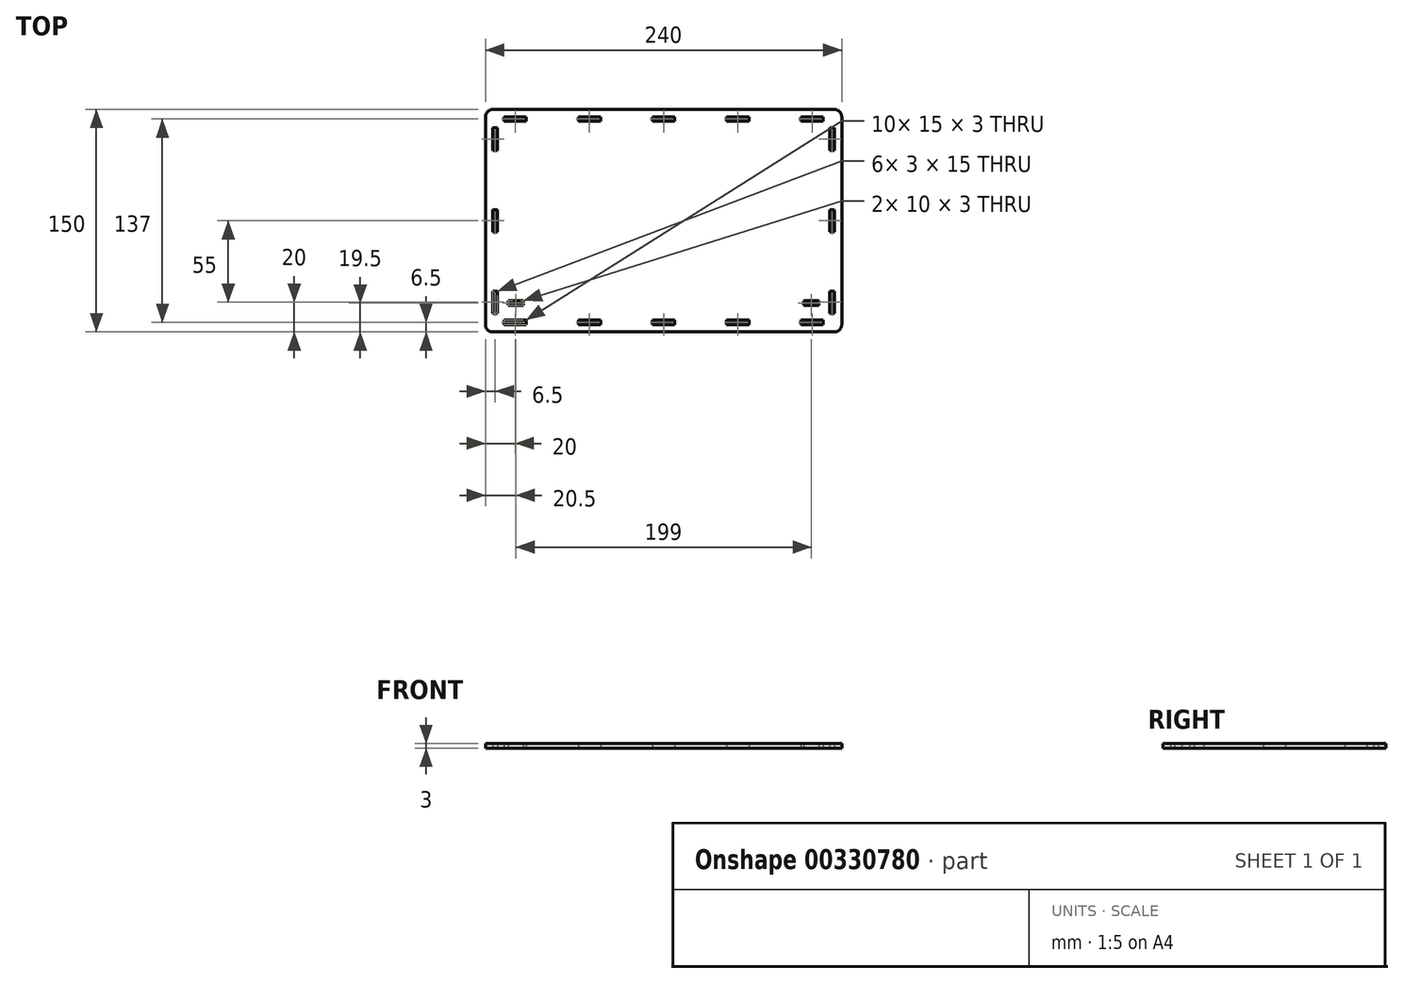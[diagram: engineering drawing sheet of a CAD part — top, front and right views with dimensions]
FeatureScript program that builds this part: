
annotation { "Feature Type Name" : "Feature", "Feature Type Description" : "" }
export const myFeature = defineFeature(function(context is Context, id is Id, definition is map)
    precondition{}
    {
        {
            var Q0;
            Q0=qCreatedBy(makeId("Top.planeOp"),FACE);
            var sketch = newSketch(context, id + "F0", { "sketchPlane" : qUnion([Q0])});
            skLineSegment(sketch, "E0.bottom", {"start": v(115, 75) * mm, "end": v(-115, 75) * mm});
            skLineSegment(sketch, "E0.top", {"start": v(115, -75) * mm, "end": v(-115, -75) * mm});
            skLineSegment(sketch, "E0.left", {"start": v(120, 70) * mm, "end": v(120, -70) * mm});
            skLineSegment(sketch, "E0.right", {"start": v(-120, 70) * mm, "end": v(-120, -70) * mm});
            skPoint(sketch, "E0.middle", {"position": v(0, 0) * mm});
            skLineSegment(sketch, "E1.bottom", {"start": v(-107.5, 70) * mm, "end": v(-92.5, 70) * mm});
            skLineSegment(sketch, "E1.top", {"start": v(-107.5, 67) * mm, "end": v(-92.5, 67) * mm});
            skLineSegment(sketch, "E1.left", {"start": v(-107.5, 70) * mm, "end": v(-107.5, 67) * mm});
            skLineSegment(sketch, "E1.right", {"start": v(-92.5, 70) * mm, "end": v(-92.5, 67) * mm});
            skLineSegment(sketch, "E2.0.1.0", {"start": v(-107.5, -67) * mm, "end": v(-107.5, -70) * mm});
            skLineSegment(sketch, "E2.0.1.1", {"start": v(-107.5, -67) * mm, "end": v(-92.5, -67) * mm});
            skLineSegment(sketch, "E2.0.1.2", {"start": v(-92.5, -67) * mm, "end": v(-92.5, -70) * mm});
            skLineSegment(sketch, "E2.0.1.3", {"start": v(-107.5, -70) * mm, "end": v(-92.5, -70) * mm});
            skLineSegment(sketch, "E2.1.0.0", {"start": v(-57.5, 70) * mm, "end": v(-57.5, 67) * mm});
            skLineSegment(sketch, "E2.1.0.1", {"start": v(-57.5, 70) * mm, "end": v(-42.5, 70) * mm});
            skLineSegment(sketch, "E2.1.0.2", {"start": v(-42.5, 70) * mm, "end": v(-42.5, 67) * mm});
            skLineSegment(sketch, "E2.1.0.3", {"start": v(-57.5, 67) * mm, "end": v(-42.5, 67) * mm});
            skLineSegment(sketch, "E2.1.1.0", {"start": v(-57.5, -67) * mm, "end": v(-57.5, -70) * mm});
            skLineSegment(sketch, "E2.1.1.1", {"start": v(-57.5, -67) * mm, "end": v(-42.5, -67) * mm});
            skLineSegment(sketch, "E2.1.1.2", {"start": v(-42.5, -67) * mm, "end": v(-42.5, -70) * mm});
            skLineSegment(sketch, "E2.1.1.3", {"start": v(-57.5, -70) * mm, "end": v(-42.5, -70) * mm});
            skLineSegment(sketch, "E2.2.0.0", {"start": v(-7.5, 70) * mm, "end": v(-7.5, 67) * mm});
            skLineSegment(sketch, "E2.2.0.1", {"start": v(-7.5, 70) * mm, "end": v(7.5, 70) * mm});
            skLineSegment(sketch, "E2.2.0.2", {"start": v(7.5, 70) * mm, "end": v(7.5, 67) * mm});
            skLineSegment(sketch, "E2.2.0.3", {"start": v(-7.5, 67) * mm, "end": v(7.5, 67) * mm});
            skLineSegment(sketch, "E2.2.1.0", {"start": v(-7.5, -67) * mm, "end": v(-7.5, -70) * mm});
            skLineSegment(sketch, "E2.2.1.1", {"start": v(-7.5, -67) * mm, "end": v(7.5, -67) * mm});
            skLineSegment(sketch, "E2.2.1.2", {"start": v(7.5, -67) * mm, "end": v(7.5, -70) * mm});
            skLineSegment(sketch, "E2.2.1.3", {"start": v(-7.5, -70) * mm, "end": v(7.5, -70) * mm});
            skLineSegment(sketch, "E2.3.0.0", {"start": v(42.5, 70) * mm, "end": v(42.5, 67) * mm});
            skLineSegment(sketch, "E2.3.0.1", {"start": v(42.5, 70) * mm, "end": v(57.5, 70) * mm});
            skLineSegment(sketch, "E2.3.0.2", {"start": v(57.5, 70) * mm, "end": v(57.5, 67) * mm});
            skLineSegment(sketch, "E2.3.0.3", {"start": v(42.5, 67) * mm, "end": v(57.5, 67) * mm});
            skLineSegment(sketch, "E2.3.1.0", {"start": v(42.5, -67) * mm, "end": v(42.5, -70) * mm});
            skLineSegment(sketch, "E2.3.1.1", {"start": v(42.5, -67) * mm, "end": v(57.5, -67) * mm});
            skLineSegment(sketch, "E2.3.1.2", {"start": v(57.5, -67) * mm, "end": v(57.5, -70) * mm});
            skLineSegment(sketch, "E2.3.1.3", {"start": v(42.5, -70) * mm, "end": v(57.5, -70) * mm});
            skLineSegment(sketch, "E2.direction1", {"start": v(-107.5, 67) * mm, "end": v(-57.5, 67) * mm, "construction": true});
            skLineSegment(sketch, "E2.direction2", {"start": v(-107.5, 67) * mm, "end": v(-107.5, -70) * mm, "construction": true});
            skLineSegment(sketch, "E3.0.4.0", {"start": v(92.5, 70) * mm, "end": v(92.5, 67) * mm});
            skLineSegment(sketch, "E3.3.4.0", {"start": v(92.5, 70) * mm, "end": v(107.5, 70) * mm});
            skLineSegment(sketch, "E3.6.4.0", {"start": v(107.5, 70) * mm, "end": v(107.5, 67) * mm});
            skLineSegment(sketch, "E3.9.4.0", {"start": v(92.5, 67) * mm, "end": v(107.5, 67) * mm});
            skLineSegment(sketch, "E3.0.4.1", {"start": v(92.5, -67) * mm, "end": v(92.5, -70) * mm});
            skLineSegment(sketch, "E3.3.4.1", {"start": v(92.5, -67) * mm, "end": v(107.5, -67) * mm});
            skLineSegment(sketch, "E3.6.4.1", {"start": v(107.5, -67) * mm, "end": v(107.5, -70) * mm});
            skLineSegment(sketch, "E3.9.4.1", {"start": v(92.5, -70) * mm, "end": v(107.5, -70) * mm});
            skPoint(sketch, "E4.visualSharp", {"position": v(-120, 75) * mm});
            skArc(sketch, "E4.filletArc", {"start": v(-115, 75) * mm, "mid": v(-118.54, 73.54) * mm, "end": v(-120, 70) * mm});
            skPoint(sketch, "E5.visualSharp", {"position": v(-120, -75) * mm});
            skArc(sketch, "E5.filletArc", {"start": v(-120, -70) * mm, "mid": v(-118.54, -73.54) * mm, "end": v(-115, -75) * mm});
            skPoint(sketch, "E6.visualSharp", {"position": v(120, -75) * mm});
            skArc(sketch, "E6.filletArc", {"start": v(115, -75) * mm, "mid": v(118.54, -73.54) * mm, "end": v(120, -70) * mm});
            skPoint(sketch, "E7.visualSharp", {"position": v(120, 75) * mm});
            skArc(sketch, "E7.filletArc", {"start": v(120, 70) * mm, "mid": v(118.54, 73.54) * mm, "end": v(115, 75) * mm});
            skLineSegment(sketch, "E8.bottom", {"start": v(112, 62.5) * mm, "end": v(115, 62.5) * mm});
            skLineSegment(sketch, "E8.top", {"start": v(112, 47.5) * mm, "end": v(115, 47.5) * mm});
            skLineSegment(sketch, "E8.left", {"start": v(112, 62.5) * mm, "end": v(112, 47.5) * mm});
            skLineSegment(sketch, "E8.right", {"start": v(115, 62.5) * mm, "end": v(115, 47.5) * mm});
            skLineSegment(sketch, "E9.0.1.0", {"start": v(112, 7.5) * mm, "end": v(115, 7.5) * mm});
            skLineSegment(sketch, "E9.0.1.1", {"start": v(115, 7.5) * mm, "end": v(115, -7.5) * mm});
            skLineSegment(sketch, "E9.0.1.2", {"start": v(112, -7.5) * mm, "end": v(115, -7.5) * mm});
            skLineSegment(sketch, "E9.0.1.3", {"start": v(112, 7.5) * mm, "end": v(112, -7.5) * mm});
            skLineSegment(sketch, "E9.0.2.0", {"start": v(112, -47.5) * mm, "end": v(115, -47.5) * mm});
            skLineSegment(sketch, "E9.0.2.1", {"start": v(115, -47.5) * mm, "end": v(115, -62.5) * mm});
            skLineSegment(sketch, "E9.0.2.2", {"start": v(112, -62.5) * mm, "end": v(115, -62.5) * mm});
            skLineSegment(sketch, "E9.0.2.3", {"start": v(112, -47.5) * mm, "end": v(112, -62.5) * mm});
            skLineSegment(sketch, "E9.1.0.0", {"start": v(-115, 62.5) * mm, "end": v(-112, 62.5) * mm});
            skLineSegment(sketch, "E9.1.0.1", {"start": v(-112, 62.5) * mm, "end": v(-112, 47.5) * mm});
            skLineSegment(sketch, "E9.1.0.2", {"start": v(-115, 47.5) * mm, "end": v(-112, 47.5) * mm});
            skLineSegment(sketch, "E9.1.0.3", {"start": v(-115, 62.5) * mm, "end": v(-115, 47.5) * mm});
            skLineSegment(sketch, "E9.1.1.0", {"start": v(-115, 7.5) * mm, "end": v(-112, 7.5) * mm});
            skLineSegment(sketch, "E9.1.1.1", {"start": v(-112, 7.5) * mm, "end": v(-112, -7.5) * mm});
            skLineSegment(sketch, "E9.1.1.2", {"start": v(-115, -7.5) * mm, "end": v(-112, -7.5) * mm});
            skLineSegment(sketch, "E9.1.1.3", {"start": v(-115, 7.5) * mm, "end": v(-115, -7.5) * mm});
            skLineSegment(sketch, "E9.1.2.0", {"start": v(-115, -47.5) * mm, "end": v(-112, -47.5) * mm});
            skLineSegment(sketch, "E9.1.2.1", {"start": v(-112, -47.5) * mm, "end": v(-112, -62.5) * mm});
            skLineSegment(sketch, "E9.1.2.2", {"start": v(-115, -62.5) * mm, "end": v(-112, -62.5) * mm});
            skLineSegment(sketch, "E9.1.2.3", {"start": v(-115, -47.5) * mm, "end": v(-115, -62.5) * mm});
            skLineSegment(sketch, "E9.direction1", {"start": v(112, 62.5) * mm, "end": v(-115, 62.5) * mm, "construction": true});
            skLineSegment(sketch, "E9.direction2", {"start": v(112, 62.5) * mm, "end": v(112, 7.5) * mm, "construction": true});
            skLineSegment(sketch, "E10.bottom", {"start": v(-104.5, -57) * mm, "end": v(-94.5, -57) * mm});
            skLineSegment(sketch, "E10.top", {"start": v(-104.5, -54) * mm, "end": v(-94.5, -54) * mm});
            skLineSegment(sketch, "E10.left", {"start": v(-104.5, -57) * mm, "end": v(-104.5, -54) * mm});
            skLineSegment(sketch, "E10.right", {"start": v(-94.5, -57) * mm, "end": v(-94.5, -54) * mm});
            skLineSegment(sketch, "E11.bottom", {"start": v(94.5, -57) * mm, "end": v(104.5, -57) * mm});
            skLineSegment(sketch, "E11.top", {"start": v(94.5, -54) * mm, "end": v(104.5, -54) * mm});
            skLineSegment(sketch, "E11.left", {"start": v(94.5, -57) * mm, "end": v(94.5, -54) * mm});
            skLineSegment(sketch, "E11.right", {"start": v(104.5, -57) * mm, "end": v(104.5, -54) * mm});
            skSolve(sketch);
        }
        {
            var Q0;
            Q0=makeQuery(id+"F0.imprint","IMPRINT",FACE,{"disambiguationData":[TD([[makeQuery(id+"F0.imprint","IMPRINT",EDGE,{"derivedFrom":sQuery(id+"F0.wireOp",EDGE,"E0.bottom")}),1.0]])]});
            extrude(context, id + "F1", {"entities" : qUnion([Q0]), "depth" : 3 * mm});
        }
    });
